# Revit family: ВУТ_ВУЕ ПБЕ_В_Л_П
name_source: partatom
category: Оборудование
units: mm (PartAtom-declared; Revit-internal decimal feet)

## family parameters
Всегда вертикально = Да
Классификация = Нет
На основе рабочей плоскости = Нет
Общий = Нет
При загрузке вырезать с полостями = Нет
Размер круглого соединителя = Использовать диаметр
Тип детали = Нормальный
Точка принадлежности помещению = Нет

## types (24) — shared parameters
00_20_Виробник = Вентс
00_20_Назва = Припливно-витяжна установка
URL = https://vents.ua
Изготовитель = Вентс
Клас фільтрації = G4
Класифікація навантаження = HVAC
Матеріал зони обслуговуваня = <По категории>
Матеріал корпусу = Сталь, гальванізована
Частота = 50 Гц
zero-valued in all types: Отметка по умолчанию

## per-type parameters (varying)
- ВУЕ 300 ПБЕ ЕС Л А21 ДТВ: 2000=Нет; 2000 ПБВ=Нет; B=485 мм; B3=135 мм; B31=350 мм; DW=12 мм; Dn=155 мм; Dy=160 мм; EB=510 мм; EB1=268 мм; EB2=50 мм; H=280 мм; H1=129 мм; H2=590 мм; HW1=120 мм; HW2=273 мм; L=1238 мм; L1=1291 мм; LW1=254 мм; LW2=219 мм; b=243 мм; Вага=44.00 кг; Висота=280 мм; Довжина=1291 мм; Діаметр=160 мм; Кількість фаз=1; Левое исполнение=Да; Максимальний потік повітря=340.0 м³/ч; Напруга=230 В; ПБВ левое=Нет; ПБВ правое=Нет; Потужність=1680 Вт; Правое исполнение=Нет; Пресостат левый=Да; Рівень звукового тиску на відстані 3 м=27 дБА; Струм=8 А; Установлена потужність=1817 В·А; Ширина=485 мм
- ВУТ 300 ПБЕ ЕС Л А21 ДТВ: 2000=Нет; 2000 ПБВ=Нет; B=485 мм; B3=135 мм; B31=350 мм; DW=12 мм; Dn=155 мм; Dy=160 мм; EB=510 мм; EB1=268 мм; EB2=50 мм; H=280 мм; H1=129 мм; H2=590 мм; HW1=120 мм; HW2=273 мм; L=1238 мм; L1=1291 мм; LW1=254 мм; LW2=219 мм; b=243 мм; Вага=44.00 кг; Висота=280 мм; Довжина=1291 мм; Діаметр=160 мм; Кількість фаз=1; Левое исполнение=Да; Максимальний потік повітря=340.0 м³/ч; Напруга=230 В; ПБВ левое=Нет; ПБВ правое=Нет; Потужність=1680 Вт; Правое исполнение=Нет; Пресостат левый=Да; Рівень звукового тиску на відстані 3 м=27 дБА; Струм=8 А; Установлена потужність=1817 В·А; Ширина=485 мм
- ВУЕ 300 ПБЕ ЕС П А21 ДТВ: 2000=Нет; 2000 ПБВ=Нет; B=485 мм; B3=350 мм; B31=135 мм; DW=12 мм; Dn=155 мм; Dy=160 мм; EB=510 мм; EB1=268 мм; EB2=50 мм; H=280 мм; H1=129 мм; H2=590 мм; HW1=120 мм; HW2=273 мм; L=1238 мм; L1=1291 мм; LW1=254 мм; LW2=219 мм; b=243 мм; Вага=44.00 кг; Висота=280 мм; Довжина=1291 мм; Діаметр=160 мм; Кількість фаз=1; Левое исполнение=Нет; Максимальний потік повітря=340.0 м³/ч; Напруга=230 В; ПБВ левое=Нет; ПБВ правое=Нет; Потужність=1680 Вт; Правое исполнение=Да; Пресостат левый=Да; Рівень звукового тиску на відстані 3 м=27 дБА; Струм=8 А; Установлена потужність=1817 В·А; Ширина=485 мм
- ВУТ 300 ПБЕ ЕС П А21 ДТВ: 2000=Нет; 2000 ПБВ=Нет; B=485 мм; B3=350 мм; B31=135 мм; DW=12 мм; Dn=155 мм; Dy=160 мм; EB=510 мм; EB1=268 мм; EB2=50 мм; H=280 мм; H1=129 мм; H2=590 мм; HW1=120 мм; HW2=273 мм; L=1238 мм; L1=1291 мм; LW1=254 мм; LW2=219 мм; b=243 мм; Вага=44.00 кг; Висота=280 мм; Довжина=1291 мм; Діаметр=160 мм; Кількість фаз=1; Левое исполнение=Нет; Максимальний потік повітря=340.0 м³/ч; Напруга=230 В; ПБВ левое=Нет; ПБВ правое=Нет; Потужність=1680 Вт; Правое исполнение=Да; Пресостат левый=Да; Рівень звукового тиску на відстані 3 м=27 дБА; Струм=8 А; Установлена потужність=1817 В·А; Ширина=485 мм
- ВУЕ 550 ПБЕ ЕС Л А21 ДТВ: 2000=Нет; 2000 ПБВ=Нет; B=827 мм; B3=188 мм; B31=639 мм; DW=12 мм; Dn=195 мм; Dy=200 мм; EB=802 мм; EB1=389 мм; EB2=5 мм; H=280 мм; H1=120 мм; H2=590 мм; HW1=160 мм; HW2=250 мм; L=1238 мм; L1=1291 мм; LW1=350 мм; LW2=370 мм; b=414 мм; Вага=67.00 кг; Висота=280 мм; Довжина=1291 мм; Діаметр=200 мм; Кількість фаз=1; Левое исполнение=Да; Максимальний потік повітря=620.0 м³/ч; Напруга=230 В; ПБВ левое=Нет; ПБВ правое=Нет; Потужність=2297 Вт; Правое исполнение=Нет; Пресостат левый=Да; Рівень звукового тиску на відстані 3 м=30 дБА; Струм=11 А; Установлена потужність=2553 В·А; Ширина=827 мм
- ВУЕ 550 ПБЕ ЕС П А21 ДТВ: 2000=Нет; 2000 ПБВ=Нет; B=827 мм; B3=188 мм; B31=639 мм; DW=12 мм; Dn=195 мм; Dy=200 мм; EB=802 мм; EB1=389 мм; EB2=5 мм; H=280 мм; H1=120 мм; H2=590 мм; HW1=160 мм; HW2=250 мм; L=1238 мм; L1=1291 мм; LW1=350 мм; LW2=370 мм; b=414 мм; Вага=67.00 кг; Висота=280 мм; Довжина=1291 мм; Діаметр=200 мм; Кількість фаз=1; Левое исполнение=Нет; Максимальний потік повітря=620.0 м³/ч; Напруга=230 В; ПБВ левое=Нет; ПБВ правое=Нет; Потужність=2297 Вт; Правое исполнение=Да; Пресостат левый=Да; Рівень звукового тиску на відстані 3 м=30 дБА; Струм=11 А; Установлена потужність=2553 В·А; Ширина=827 мм
- ВУТ 550 ПБЕ ЕС Л А21 ДТВ: 2000=Нет; 2000 ПБВ=Нет; B=827 мм; B3=188 мм; B31=639 мм; DW=12 мм; Dn=195 мм; Dy=200 мм; EB=802 мм; EB1=389 мм; EB2=5 мм; H=280 мм; H1=120 мм; H2=590 мм; HW1=160 мм; HW2=250 мм; L=1238 мм; L1=1291 мм; LW1=350 мм; LW2=370 мм; b=414 мм; Вага=67.00 кг; Висота=280 мм; Довжина=1291 мм; Діаметр=200 мм; Кількість фаз=1; Левое исполнение=Да; Максимальний потік повітря=620.0 м³/ч; Напруга=230 В; ПБВ левое=Нет; ПБВ правое=Нет; Потужність=2297 Вт; Правое исполнение=Нет; Пресостат левый=Да; Рівень звукового тиску на відстані 3 м=30 дБА; Струм=11 А; Установлена потужність=2553 В·А; Ширина=827 мм
- ВУТ 550 ПБЕ ЕС П А21 ДТВ: 2000=Нет; 2000 ПБВ=Нет; B=827 мм; B3=188 мм; B31=639 мм; DW=12 мм; Dn=195 мм; Dy=200 мм; EB=802 мм; EB1=389 мм; EB2=5 мм; H=280 мм; H1=120 мм; H2=590 мм; HW1=160 мм; HW2=250 мм; L=1238 мм; L1=1291 мм; LW1=350 мм; LW2=370 мм; b=414 мм; Вага=67.00 кг; Висота=280 мм; Довжина=1291 мм; Діаметр=200 мм; Кількість фаз=1; Левое исполнение=Нет; Максимальний потік повітря=620.0 м³/ч; Напруга=230 В; ПБВ левое=Нет; ПБВ правое=Нет; Потужність=2297 Вт; Правое исполнение=Да; Пресостат левый=Да; Рівень звукового тиску на відстані 3 м=30 дБА; Струм=11 А; Установлена потужність=2553 В·А; Ширина=827 мм
- ВУЕ 900 ПБЕ ЕС Л А21 ДТВ: 2000=Нет; 2000 ПБВ=Нет; B=1351 мм; B3=350 мм; B31=1080 мм; DW=20 мм; Dn=245 мм; Dy=250 мм; EB=1326 мм; EB1=651 мм; EB2=5 мм; H=318 мм; H1=143 мм; H2=590 мм; HW1=50 мм; HW2=265 мм; L=1349 мм; L1=1402 мм; LW1=70 мм; LW2=135 мм; b=676 мм; Вага=111.00 кг; Висота=318 мм; Довжина=1402 мм; Діаметр=250 мм; Кількість фаз=1; Левое исполнение=Да; Максимальний потік повітря=1030.0 м³/ч; Напруга=230 В; ПБВ левое=Нет; ПБВ правое=Нет; Потужність=3742 Вт; Правое исполнение=Нет; Пресостат левый=Да; Рівень звукового тиску на відстані 3 м=33 дБА; Струм=17 А; Установлена потужність=4002 В·А; Ширина=1351 мм
- ВУЕ 900 ПБЕ ЕС П А21 ДТВ: 2000=Нет; 2000 ПБВ=Нет; B=1351 мм; B3=430 мм; B31=1080 мм; DW=20 мм; Dn=245 мм; Dy=250 мм; EB=1326 мм; EB1=651 мм; EB2=5 мм; H=318 мм; H1=143 мм; H2=590 мм; HW1=50 мм; HW2=265 мм; L=1349 мм; L1=1402 мм; LW1=70 мм; LW2=135 мм; b=676 мм; Вага=111.00 кг; Висота=318 мм; Довжина=1402 мм; Діаметр=250 мм; Кількість фаз=1; Левое исполнение=Нет; Максимальний потік повітря=1030.0 м³/ч; Напруга=230 В; ПБВ левое=Нет; ПБВ правое=Нет; Потужність=3742 Вт; Правое исполнение=Да; Пресостат левый=Да; Рівень звукового тиску на відстані 3 м=33 дБА; Струм=17 А; Установлена потужність=4002 В·А; Ширина=1351 мм
- ВУТ 900 ПБЕ ЕС Л А21 ДТВ: 2000=Нет; 2000 ПБВ=Нет; B=1351 мм; B3=350 мм; B31=1080 мм; DW=20 мм; Dn=245 мм; Dy=250 мм; EB=1326 мм; EB1=651 мм; EB2=5 мм; H=318 мм; H1=143 мм; H2=590 мм; HW1=50 мм; HW2=265 мм; L=1349 мм; L1=1402 мм; LW1=70 мм; LW2=135 мм; b=676 мм; Вага=111.00 кг; Висота=318 мм; Довжина=1402 мм; Діаметр=250 мм; Кількість фаз=1; Левое исполнение=Да; Максимальний потік повітря=1030.0 м³/ч; Напруга=230 В; ПБВ левое=Нет; ПБВ правое=Нет; Потужність=3742 Вт; Правое исполнение=Нет; Пресостат левый=Да; Рівень звукового тиску на відстані 3 м=33 дБА; Струм=17 А; Установлена потужність=4002 В·А; Ширина=1351 мм
- ВУТ 900 ПБЕ ЕС П А21 ДТВ: 2000=Нет; 2000 ПБВ=Нет; B=1351 мм; B3=430 мм; B31=1080 мм; DW=20 мм; Dn=245 мм; Dy=250 мм; EB=1326 мм; EB1=651 мм; EB2=5 мм; H=318 мм; H1=143 мм; H2=590 мм; HW1=50 мм; HW2=265 мм; L=1349 мм; L1=1402 мм; LW1=70 мм; LW2=135 мм; b=676 мм; Вага=111.00 кг; Висота=318 мм; Довжина=1402 мм; Діаметр=250 мм; Кількість фаз=1; Левое исполнение=Нет; Максимальний потік повітря=1030.0 м³/ч; Напруга=230 В; ПБВ левое=Нет; ПБВ правое=Нет; Потужність=3742 Вт; Правое исполнение=Да; Пресостат левый=Да; Рівень звукового тиску на відстані 3 м=33 дБА; Струм=17 А; Установлена потужність=4002 В·А; Ширина=1351 мм
- ВУЕ 550 ПБВ ЕС Л А21 ДТВ: 2000=Нет; 2000 ПБВ=Нет; B=827 мм; B3=188 мм; B31=639 мм; DW=12 мм; Dn=195 мм; Dy=200 мм; EB=802 мм; EB1=389 мм; EB2=5 мм; H=280 мм; H1=120 мм; H2=590 мм; HW1=160 мм; HW2=250 мм; L=1238 мм; L1=1291 мм; LW1=350 мм; LW2=370 мм; b=414 мм; Вага=68.00 кг; Висота=280 мм; Довжина=1291 мм; Діаметр=200 мм; Кількість фаз=1; Левое исполнение=Да; Максимальний потік повітря=620.0 м³/ч; Напруга=230 В; ПБВ левое=Да; ПБВ правое=Нет; Потужність=297 Вт; Правое исполнение=Нет; Пресостат левый=Да; Рівень звукового тиску на відстані 3 м=30 дБА; Струм=2 А; Установлена потужність=552 В·А; Ширина=827 мм
- ВУТ 550 ПБВ ЕС Л А21 ДТВ: 2000=Нет; 2000 ПБВ=Нет; B=827 мм; B3=188 мм; B31=639 мм; DW=12 мм; Dn=195 мм; Dy=200 мм; EB=802 мм; EB1=389 мм; EB2=5 мм; H=280 мм; H1=120 мм; H2=590 мм; HW1=160 мм; HW2=250 мм; L=1238 мм; L1=1291 мм; LW1=350 мм; LW2=370 мм; b=414 мм; Вага=68.00 кг; Висота=280 мм; Довжина=1291 мм; Діаметр=200 мм; Кількість фаз=1; Левое исполнение=Да; Максимальний потік повітря=620.0 м³/ч; Напруга=230 В; ПБВ левое=Да; ПБВ правое=Нет; Потужність=297 Вт; Правое исполнение=Нет; Пресостат левый=Да; Рівень звукового тиску на відстані 3 м=30 дБА; Струм=2 А; Установлена потужність=552 В·А; Ширина=827 мм
- ВУЕ 550 ПБВ ЕС П А21 ДТВ: 2000=Нет; 2000 ПБВ=Нет; B=827 мм; B3=188 мм; B31=639 мм; DW=12 мм; Dn=195 мм; Dy=200 мм; EB=802 мм; EB1=389 мм; EB2=5 мм; H=280 мм; H1=120 мм; H2=590 мм; HW1=160 мм; HW2=250 мм; L=1238 мм; L1=1291 мм; LW1=350 мм; LW2=370 мм; b=414 мм; Вага=68.00 кг; Висота=280 мм; Довжина=1291 мм; Діаметр=200 мм; Кількість фаз=1; Левое исполнение=Нет; Максимальний потік повітря=620.0 м³/ч; Напруга=230 В; ПБВ левое=Нет; ПБВ правое=Да; Потужність=297 Вт; Правое исполнение=Да; Пресостат левый=Да; Рівень звукового тиску на відстані 3 м=30 дБА; Струм=2 А; Установлена потужність=552 В·А; Ширина=827 мм
- ВУТ 550 ПБВ ЕС П А21 ДТВ: 2000=Нет; 2000 ПБВ=Нет; B=827 мм; B3=188 мм; B31=639 мм; DW=12 мм; Dn=195 мм; Dy=200 мм; EB=802 мм; EB1=389 мм; EB2=5 мм; H=280 мм; H1=120 мм; H2=590 мм; HW1=160 мм; HW2=250 мм; L=1238 мм; L1=1291 мм; LW1=350 мм; LW2=370 мм; b=414 мм; Вага=68.00 кг; Висота=280 мм; Довжина=1291 мм; Діаметр=200 мм; Кількість фаз=1; Левое исполнение=Нет; Максимальний потік повітря=620.0 м³/ч; Напруга=230 В; ПБВ левое=Нет; ПБВ правое=Да; Потужність=297 Вт; Правое исполнение=Да; Пресостат левый=Да; Рівень звукового тиску на відстані 3 м=30 дБА; Струм=2 А; Установлена потужність=552 В·А; Ширина=827 мм
- ВУЕ 900 ПБВ ЕС Л А21 ДТВ: 2000=Нет; 2000 ПБВ=Нет; B=1351 мм; B3=350 мм; B31=1080 мм; DW=20 мм; Dn=245 мм; Dy=250 мм; EB=1326 мм; EB1=651 мм; EB2=5 мм; H=318 мм; H1=143 мм; H2=590 мм; HW1=50 мм; HW2=265 мм; L=1349 мм; L1=1402 мм; LW1=70 мм; LW2=135 мм; b=676 мм; Вага=112.00 кг; Висота=318 мм; Довжина=1402 мм; Діаметр=250 мм; Кількість фаз=1; Левое исполнение=Да; Максимальний потік повітря=1030.0 м³/ч; Напруга=230 В; ПБВ левое=Да; ПБВ правое=Нет; Потужність=442 Вт; Правое исполнение=Нет; Пресостат левый=Да; Рівень звукового тиску на відстані 3 м=33 дБА; Струм=3 А; Установлена потужність=690 В·А; Ширина=1351 мм
- ВУТ 900 ПБВ ЕС Л А21 ДТВ: 2000=Нет; 2000 ПБВ=Нет; B=1351 мм; B3=350 мм; B31=1080 мм; DW=20 мм; Dn=245 мм; Dy=250 мм; EB=1326 мм; EB1=651 мм; EB2=5 мм; H=318 мм; H1=143 мм; H2=590 мм; HW1=50 мм; HW2=265 мм; L=1349 мм; L1=1402 мм; LW1=70 мм; LW2=135 мм; b=676 мм; Вага=112.00 кг; Висота=318 мм; Довжина=1402 мм; Діаметр=250 мм; Кількість фаз=1; Левое исполнение=Да; Максимальний потік повітря=1030.0 м³/ч; Напруга=230 В; ПБВ левое=Да; ПБВ правое=Нет; Потужність=442 Вт; Правое исполнение=Нет; Пресостат левый=Да; Рівень звукового тиску на відстані 3 м=33 дБА; Струм=3 А; Установлена потужність=690 В·А; Ширина=1351 мм
- ВУЕ 900 ПБВ ЕС П А21 ДТВ: 2000=Нет; 2000 ПБВ=Нет; B=1351 мм; B3=430 мм; B31=1080 мм; DW=20 мм; Dn=245 мм; Dy=250 мм; EB=1326 мм; EB1=651 мм; EB2=5 мм; H=318 мм; H1=143 мм; H2=590 мм; HW1=50 мм; HW2=265 мм; L=1349 мм; L1=1402 мм; LW1=70 мм; LW2=135 мм; b=676 мм; Вага=112.00 кг; Висота=318 мм; Довжина=1402 мм; Діаметр=250 мм; Кількість фаз=1; Левое исполнение=Нет; Максимальний потік повітря=1030.0 м³/ч; Напруга=230 В; ПБВ левое=Нет; ПБВ правое=Да; Потужність=442 Вт; Правое исполнение=Да; Пресостат левый=Да; Рівень звукового тиску на відстані 3 м=33 дБА; Струм=3 А; Установлена потужність=690 В·А; Ширина=1351 мм
- ВУТ 900 ПБВ ЕС П А21 ДТВ: 2000=Нет; 2000 ПБВ=Нет; B=1351 мм; B3=430 мм; B31=1080 мм; DW=20 мм; Dn=245 мм; Dy=250 мм; EB=1326 мм; EB1=651 мм; EB2=5 мм; H=318 мм; H1=143 мм; H2=590 мм; HW1=50 мм; HW2=265 мм; L=1349 мм; L1=1402 мм; LW1=70 мм; LW2=135 мм; b=676 мм; Вага=112.00 кг; Висота=318 мм; Довжина=1402 мм; Діаметр=250 мм; Кількість фаз=1; Левое исполнение=Нет; Максимальний потік повітря=1030.0 м³/ч; Напруга=230 В; ПБВ левое=Нет; ПБВ правое=Да; Потужність=442 Вт; Правое исполнение=Да; Пресостат левый=Да; Рівень звукового тиску на відстані 3 м=33 дБА; Струм=3 А; Установлена потужність=690 В·А; Ширина=1351 мм
- ВУТ 2000 ПБЕ ЕС А21 ДТВ: 2000=Да; 2000 ПБВ=Нет; B=950 мм; B3=225 мм; B31=725 мм; DW=20 мм; Dn=310 мм; Dy=315 мм; EB=925 мм; EB1=450 мм; EB2=5 мм; H=762 мм; H1=367 мм; H2=690 мм; HW1=50 мм; HW2=265 мм; L=1400 мм; L1=1453 мм; LW1=70 мм; LW2=135 мм; b=475 мм; Вага=140.00 кг; Висота=762 мм; Довжина=1453 мм; Діаметр=315 мм; Кількість фаз=3; Левое исполнение=Да; Максимальний потік повітря=2100.0 м³/ч; Напруга=400 В; ПБВ левое=Нет; ПБВ правое=Нет; Потужність=15876 Вт; Правое исполнение=Нет; Пресостат левый=Нет; Рівень звукового тиску на відстані 3 м=36 дБА; Струм=27 А; Установлена потужність=10800 В·А; Ширина=950 мм
- ВУТ 3000 ПБЕ ЕС А21 ДТВ: 2000=Да; 2000 ПБВ=Нет; B=1265 мм; B3=347 мм; B31=918 мм; DW=20 мм; Dn=395 мм; Dy=400 мм; EB=1240 мм; EB1=608 мм; EB2=5 мм; H=881 мм; H1=427 мм; H2=590 мм; HW1=50 мм; HW2=265 мм; L=1835 мм; L1=1888 мм; LW1=70 мм; LW2=135 мм; b=633 мм; Вага=281.00 кг; Висота=881 мм; Довжина=1888 мм; Діаметр=400 мм; Кількість фаз=3; Левое исполнение=Да; Максимальний потік повітря=4300.0 м³/ч; Напруга=400 В; ПБВ левое=Нет; ПБВ правое=Нет; Потужність=23226 Вт; Правое исполнение=Нет; Пресостат левый=Нет; Рівень звукового тиску на відстані 3 м=46 дБА; Струм=34 А; Установлена потужність=13400 В·А; Ширина=1265 мм
- ВУТ 2000 ПБВ ЕС А21 ДТВ: 2000=Да; 2000 ПБВ=Да; B=950 мм; B3=225 мм; B31=725 мм; DW=20 мм; Dn=310 мм; Dy=315 мм; EB=925 мм; EB1=450 мм; EB2=5 мм; H=762 мм; H1=367 мм; H2=690 мм; HW1=50 мм; HW2=265 мм; L=1400 мм; L1=1453 мм; LW1=70 мм; LW2=135 мм; b=475 мм; Вага=140.00 кг; Висота=762 мм; Довжина=1453 мм; Діаметр=315 мм; Кількість фаз=1; Левое исполнение=Да; Максимальний потік повітря=2100.0 м³/ч; Напруга=230 В; ПБВ левое=Нет; ПБВ правое=Нет; Потужність=876 Вт; Правое исполнение=Нет; Пресостат левый=Нет; Рівень звукового тиску на відстані 3 м=36 дБА; Струм=5 А; Установлена потужність=1219 В·А; Ширина=950 мм
- ВУТ 3000 ПБВ ЕС А21 ДТВ: 2000=Да; 2000 ПБВ=Да; B=1265 мм; B3=347 мм; B31=918 мм; DW=20 мм; Dn=395 мм; Dy=400 мм; EB=1240 мм; EB1=608 мм; EB2=5 мм; H=881 мм; H1=427 мм; H2=590 мм; HW1=50 мм; HW2=265 мм; L=1835 мм; L1=1888 мм; LW1=70 мм; LW2=135 мм; b=633 мм; Вага=268.00 кг; Висота=881 мм; Довжина=1888 мм; Діаметр=400 мм; Кількість фаз=3; Левое исполнение=Да; Максимальний потік повітря=4300.0 м³/ч; Напруга=400 В; ПБВ левое=Нет; ПБВ правое=Нет; Потужність=2226 Вт; Правое исполнение=Нет; Пресостат левый=Нет; Рівень звукового тиску на відстані 3 м=46 дБА; Струм=4 А; Установлена потужність=1400 В·А; Ширина=1265 мм

note: column(s) folded — value = type name in every type: 00_20_Тип
